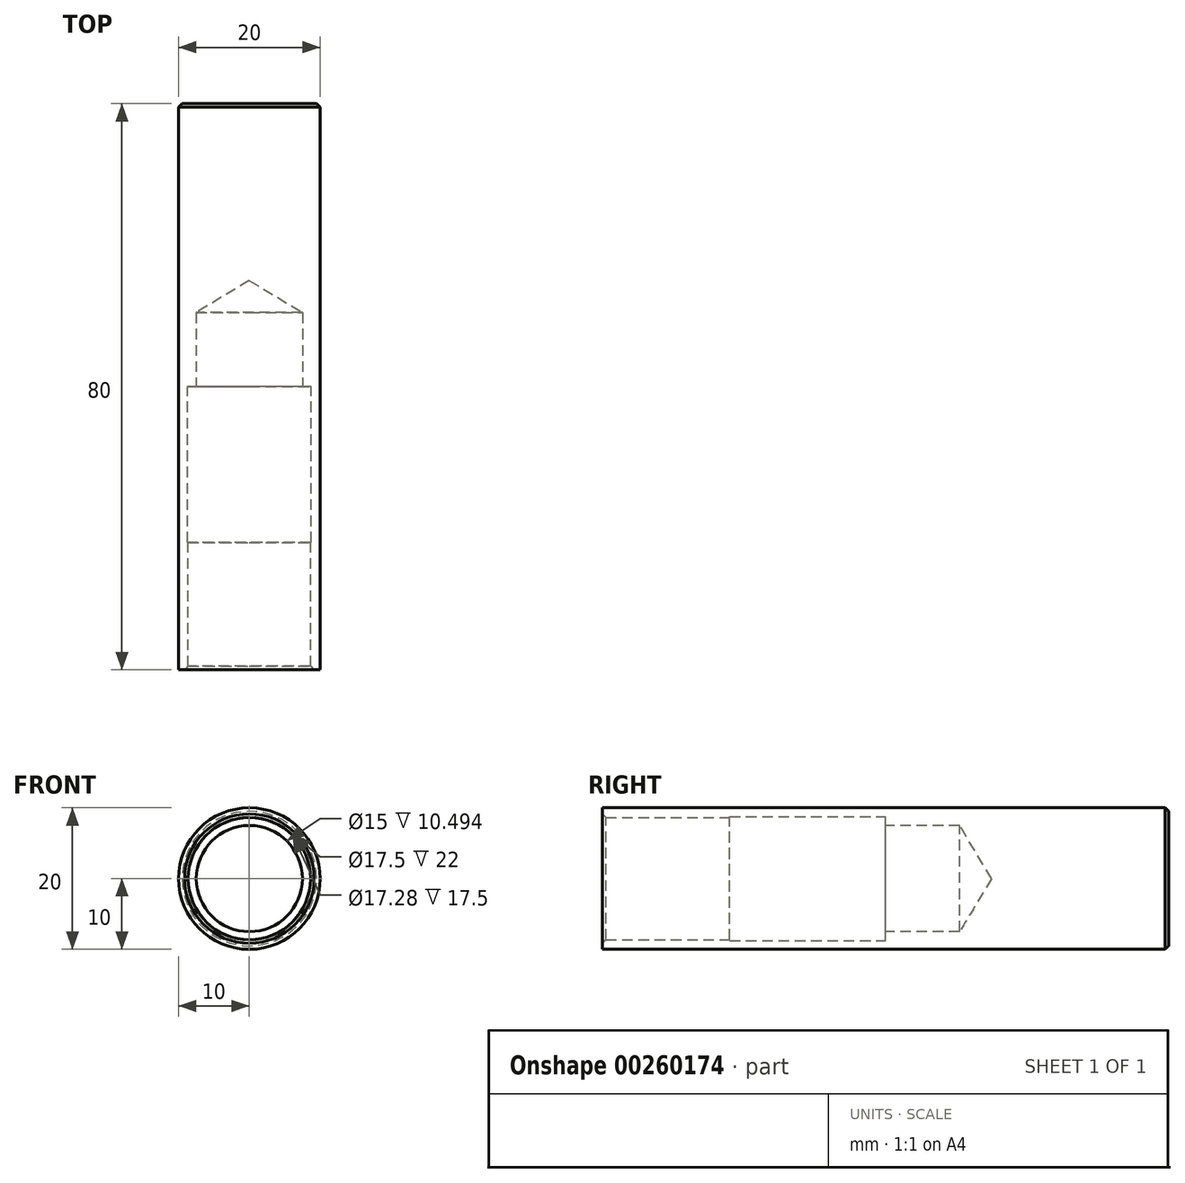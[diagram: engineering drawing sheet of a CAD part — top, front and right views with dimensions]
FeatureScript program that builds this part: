
annotation { "Feature Type Name" : "Feature", "Feature Type Description" : "" }
export const myFeature = defineFeature(function(context is Context, id is Id, definition is map)
    precondition{}
    {
        {
            var Q0;
            Q0=qCreatedBy(makeId("Front.planeOp"),FACE);
            var sketch = newSketch(context, id + "F0", { "sketchPlane" : qUnion([Q0])});
            skCircle(sketch, "E0", {"center": v(0, 0) * mm, "radius": 10 * mm});
            skSolve(sketch);
        }
        {
            var Q0;
            Q0=makeQuery(id+"F0.imprint","IMPRINT",FACE,{"disambiguationData":[TD([[makeQuery(id+"F0.imprint","IMPRINT",EDGE,{"derivedFrom":sQuery(id+"F0.wireOp",EDGE,"E0")}),1.0]])]});
            extrude(context, id + "F1", {"entities" : qUnion([Q0]), "endBound" : BoundingType.SYMMETRIC, "depth" : 40 * mm});
        }
        {
            var Q0;
            Q0=makeQuery(id+"F1.opExtrude","CAP_FACE",FACE,{"disambiguationData":[OSD([sQuery(id+"F0.wireOp",EDGE,"E0")])],"isStart":false});
            var sketch = newSketch(context, id + "F2", { "sketchPlane" : qUnion([Q0])});
            skPoint(sketch, "E1", {"position": v(0, 0) * mm});
            skSolve(sketch);
        }
        {
            var Q0;
            Q0=sQuery(id+"F2.wireOp",VERTEX,"E1");
            var Q1;
            Q1=makeQuery(id+"F1.opExtrude","SWEPT_BODY",BODY,{"disambiguationData":[OSD([sQuery(id+"F0.wireOp",EDGE,"E0")])]});
            hole(context, id + "F3", {"style" : HoleStyle.SIMPLE, "endStyle" : HoleEndStyle.BLIND, "holeDiameter" : 15 * mm, "holeDepth" : 10.5 * mm, "tappedDepth" : 32 * mm, "tapClearance" : 3, "startFromSketch" : true, "locations" : qUnion([Q0]), "scope" : qUnion([Q1])});
        }
        {
            var Q0;
            Q0=makeQuery(id+"F1.opExtrude","CAP_FACE",FACE,{"disambiguationData":[OSD([sQuery(id+"F0.wireOp",EDGE,"E0")])],"isStart":false});
            var sketch = newSketch(context, id + "F4", { "sketchPlane" : qUnion([Q0])});
            skCircle(sketch, "E2", {"center": v(0, 0) * mm, "radius": 10 * mm});
            skCircle(sketch, "E3", {"center": v(0, 0) * mm, "radius": 8.75 * mm});
            skSolve(sketch);
        }
        {
            var Q0;
            Q0 = qSketchRegion(id + "F4", true);
            extrude(context, id + "F5", {"entities" : qUnion([Q0]), "operationType" : NewBodyOperationType.ADD, "depth" : 22 * mm});
        }
        {
            var Q0;
            Q0=makeQuery(id+"F5.opExtrude","CAP_FACE",FACE,{"disambiguationData":[OSD([sQuery(id+"F4.wireOp",EDGE,"E2"),sQuery(id+"F4.wireOp",EDGE,"E3")])],"isStart":false});
            var sketch = newSketch(context, id + "F6", { "sketchPlane" : qUnion([Q0])});
            skCircle(sketch, "E4", {"center": v(0, 0) * mm, "radius": 10 * mm});
            skCircle(sketch, "E5", {"center": v(0, 0) * mm, "radius": 8.64 * mm});
            skSolve(sketch);
        }
        {
            var Q0;
            Q0 = qSketchRegion(id + "F6", true);
            extrude(context, id + "F7", {"entities" : qUnion([Q0]), "operationType" : NewBodyOperationType.ADD, "depth" : 18 * mm});
        }
        {
            var Q0;
            Q0=makeQuery(id+"F7.opExtrude","CAP_EDGE",EDGE,{"disambiguationData":[OSD([sQuery(id+"F6.wireOp",EDGE,"E5")])],"isStart":false});
            var Q1;
            Q1=makeQuery(id+"F1.opExtrude","CAP_EDGE",EDGE,{"disambiguationData":[OSD([sQuery(id+"F0.wireOp",EDGE,"E0")])],"isStart":true});
            chamfer(context, id + "F8", {"entities" : qUnion([Q0, Q1]), "width" : 0.5 * mm, "tangentPropagation" : true});
        }
    });
